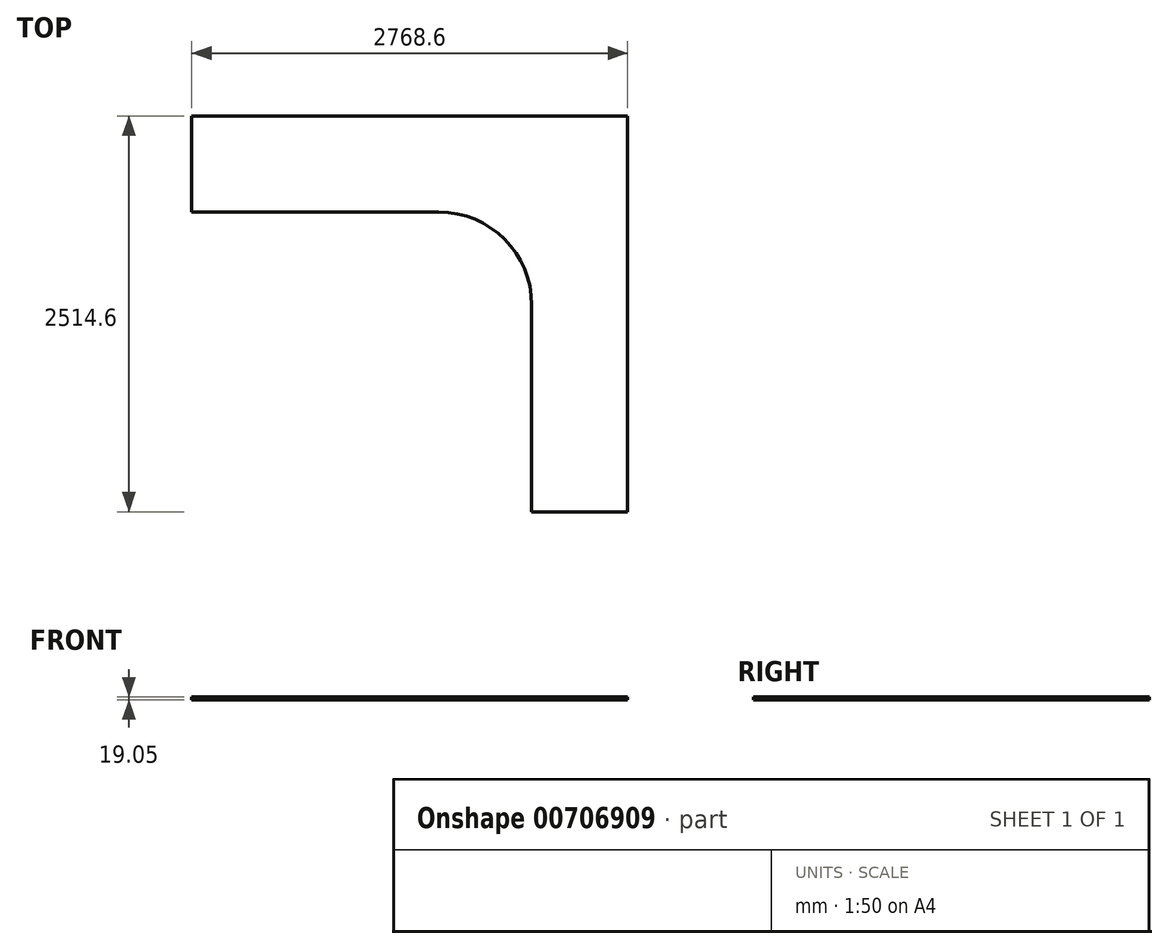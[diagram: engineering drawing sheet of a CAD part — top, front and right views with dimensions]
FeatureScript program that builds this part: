
annotation { "Feature Type Name" : "Feature", "Feature Type Description" : "" }
export const myFeature = defineFeature(function(context is Context, id is Id, definition is map)
    precondition{}
    {
        {
            var Q0;
            Q0=qCreatedBy(makeId("Top.planeOp"),FACE);
            var sketch = newSketch(context, id + "F0", { "sketchPlane" : qUnion([Q0])});
            skLineSegment(sketch, "E0.bottom", {"start": v(590.55, 0) * mm, "end": v(1200.15, 0) * mm});
            skLineSegment(sketch, "E0.top", {"start": v(0, 1200.15) * mm, "end": v(1200.15, 1200.15) * mm});
            skLineSegment(sketch, "E0.left", {"start": v(0, 590.55) * mm, "end": v(0, 1200.15) * mm});
            skLineSegment(sketch, "E0.right", {"start": v(1200.15, 0) * mm, "end": v(1200.15, 1200.15) * mm});
            skArc(sketch, "E1", {"start": v(590.55, 0) * mm, "mid": v(417.58, 417.58) * mm, "end": v(0, 590.55) * mm});
            skLineSegment(sketch, "E2.bottom", {"start": v(0, 590.55) * mm, "end": v(-1568.45, 590.55) * mm});
            skLineSegment(sketch, "E2.top", {"start": v(0, 1200.15) * mm, "end": v(-1568.45, 1200.15) * mm});
            skLineSegment(sketch, "E2.right", {"start": v(-1568.45, 590.55) * mm, "end": v(-1568.45, 1200.15) * mm});
            skLineSegment(sketch, "E3.top", {"start": v(590.55, -1314.45) * mm, "end": v(1200.15, -1314.45) * mm});
            skLineSegment(sketch, "E3.left", {"start": v(590.55, 0) * mm, "end": v(590.55, -1314.45) * mm});
            skLineSegment(sketch, "E3.right", {"start": v(1200.15, 0) * mm, "end": v(1200.15, -1314.45) * mm});
            skSolve(sketch);
        }
        {
            var Q0;
            Q0=makeQuery(id+"F0.imprint","IMPRINT",FACE,{"disambiguationData":[TD([[makeQuery(id+"F0.imprint","IMPRINT",EDGE,{"derivedFrom":sQuery(id+"F0.wireOp",EDGE,"E2.bottom")}),-1.0]])]});
            var Q1;
            Q1=makeQuery(id+"F0.imprint","IMPRINT",FACE,{"disambiguationData":[TD([[makeQuery(id+"F0.imprint","IMPRINT",EDGE,{"derivedFrom":sQuery(id+"F0.wireOp",EDGE,"E0.top")}),-1.0]])]});
            var Q2;
            Q2=makeQuery(id+"F0.imprint","IMPRINT",FACE,{"disambiguationData":[TD([[makeQuery(id+"F0.imprint","IMPRINT",EDGE,{"derivedFrom":sQuery(id+"F0.wireOp",EDGE,"E0.bottom")}),-1.0]])]});
            extrude(context, id + "F1", {"entities" : qUnion([Q0, Q1, Q2]), "depth" : 19.05 * mm, "offsetDistance" : 25.4 * mm});
        }
    });
